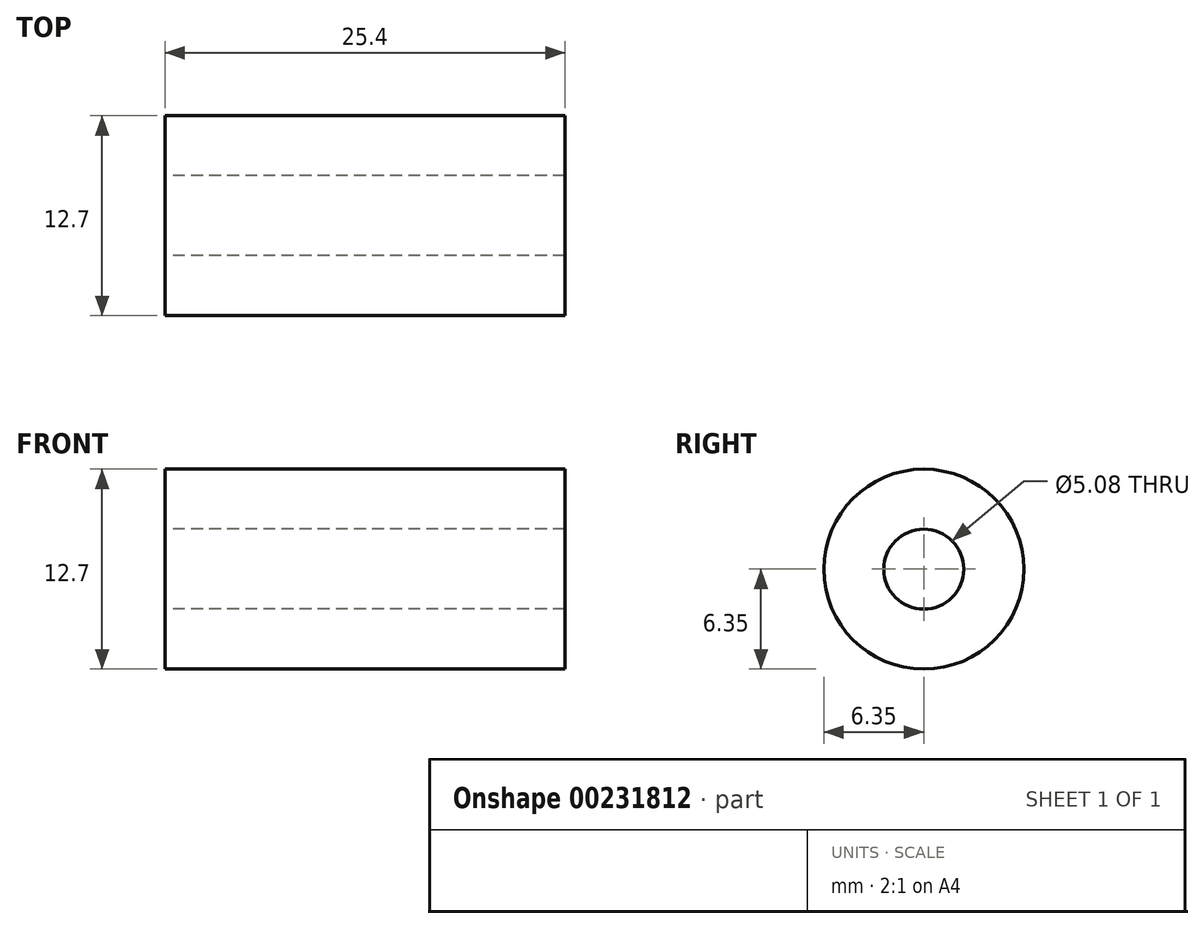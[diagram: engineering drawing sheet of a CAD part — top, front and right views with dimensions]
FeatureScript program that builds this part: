
annotation { "Feature Type Name" : "Feature", "Feature Type Description" : "" }
export const myFeature = defineFeature(function(context is Context, id is Id, definition is map)
    precondition{}
    {
        {
            var Q0;
            Q0=qCreatedBy(makeId("Right.planeOp"),FACE);
            var sketch = newSketch(context, id + "F0", { "sketchPlane" : qUnion([Q0])});
            skCircle(sketch, "E0", {"center": v(0, 0) * mm, "radius": 6.35 * mm});
            skSolve(sketch);
        }
        {
            var Q0;
            Q0 = qSketchRegion(id + "F0", true);
            extrude(context, id + "F1", {"entities" : qUnion([Q0]), "depth" : 25.4 * mm});
        }
        {
            var Q0;
            Q0=qCreatedBy(makeId("Right.planeOp"),FACE);
            var sketch = newSketch(context, id + "F2", { "sketchPlane" : qUnion([Q0])});
            skPoint(sketch, "E1", {"position": v(0, 0) * mm});
            skPoint(sketch, "E2", {"position": v(2.54, 0) * mm});
            skSolve(sketch);
        }
        {
            var Q0;
            Q0=sQuery(id+"F2.wireOp",VERTEX,"E1");
            var Q1;
            Q1=makeQuery(id+"F1.opExtrude","SWEPT_BODY",BODY,{"disambiguationData":[OSD([sQuery(id+"F0.wireOp",EDGE,"E0")])]});
            hole(context, id + "F3", {"style" : HoleStyle.SIMPLE, "endStyle" : HoleEndStyle.THROUGH, "oppositeDirection" : true, "holeDiameter" : 5.08 * mm, "startFromSketch" : true, "locations" : qUnion([Q0]), "scope" : qUnion([Q1]), "isTappedThrough" : true});
        }
    });
